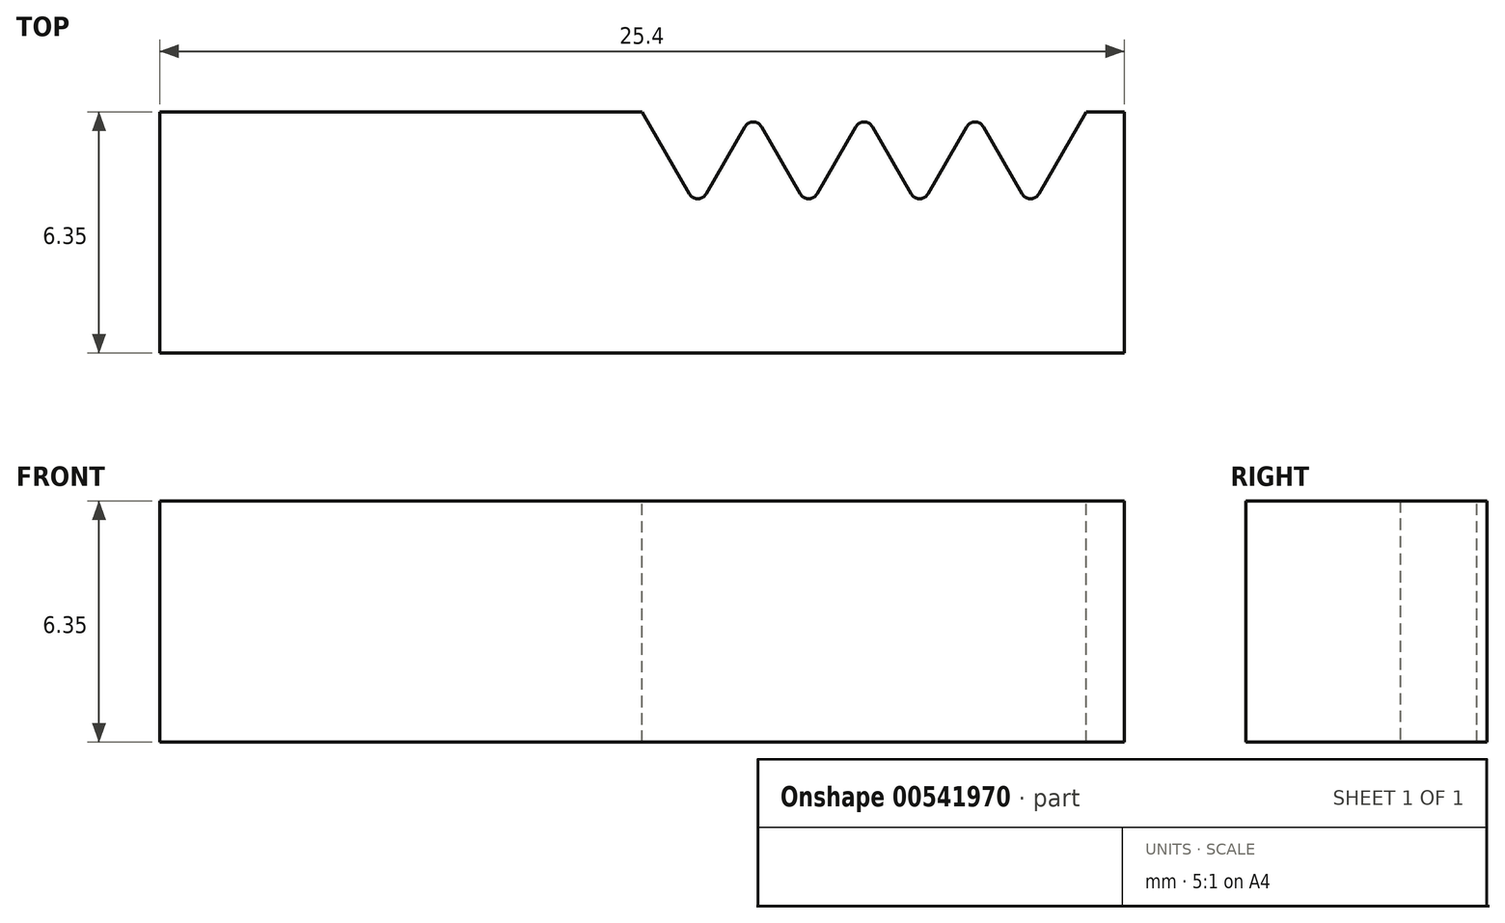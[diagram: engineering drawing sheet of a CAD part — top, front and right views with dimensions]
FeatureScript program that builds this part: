
annotation { "Feature Type Name" : "Feature", "Feature Type Description" : "" }
export const myFeature = defineFeature(function(context is Context, id is Id, definition is map)
    precondition{}
    {
        {
            var Q0;
            Q0=qCreatedBy(makeId("Top.planeOp"),FACE);
            var sketch = newSketch(context, id + "F0", { "sketchPlane" : qUnion([Q0])});
            skLineSegment(sketch, "E0", {"start": v(0, 0) * mm, "end": v(25.4, 0) * mm});
            skLineSegment(sketch, "E1", {"start": v(25.4, 0) * mm, "end": v(25.4, 6.35) * mm});
            skLineSegment(sketch, "E2", {"start": v(25.4, 6.35) * mm, "end": v(0, 6.35) * mm});
            skLineSegment(sketch, "E3", {"start": v(0, 6.35) * mm, "end": v(0, 0) * mm});
            skSolve(sketch);
        }
        {
            var Q0;
            Q0 = qSketchRegion(id + "F0", true);
            extrude(context, id + "F1", {"entities" : qUnion([Q0]), "depth" : 6.35 * mm, "offsetDistance" : 25.4 * mm});
        }
        {
            var Q0;
            Q0=makeQuery(id+"F1.opExtrude","CAP_FACE",FACE,{"disambiguationData":[OSD([sQuery(id+"F0.wireOp",EDGE,"E0"),sQuery(id+"F0.wireOp",EDGE,"E1"),sQuery(id+"F0.wireOp",EDGE,"E2"),sQuery(id+"F0.wireOp",EDGE,"E3")])],"isStart":false});
            var sketch = newSketch(context, id + "F2", { "sketchPlane" : qUnion([Q0])});
            skLineSegment(sketch, "E4", {"start": v(12.7, 0.48) * mm, "end": v(12.7, 10.56) * mm, "construction": true});
            skPoint(sketch, "E4.startSnap0", {"position": v(12.7, 0) * mm});
            skLineSegment(sketch, "E5", {"start": v(25.4, 3.81) * mm, "end": v(0, 3.8) * mm, "construction": true});
            skLineSegment(sketch, "E6", {"start": v(12.7, 6.35) * mm, "end": v(14.17, 3.8) * mm});
            skLineSegment(sketch, "E7", {"start": v(14.17, 3.8) * mm, "end": v(15.63, 6.35) * mm});
            skLineSegment(sketch, "E8.1.0.0", {"start": v(15.62, 6.35) * mm, "end": v(17.09, 3.81) * mm});
            skLineSegment(sketch, "E8.1.0.1", {"start": v(17.09, 3.8) * mm, "end": v(18.55, 6.35) * mm});
            skLineSegment(sketch, "E8.2.0.0", {"start": v(18.54, 6.35) * mm, "end": v(20, 3.81) * mm});
            skLineSegment(sketch, "E8.2.0.1", {"start": v(20, 3.8) * mm, "end": v(21.47, 6.35) * mm});
            skLineSegment(sketch, "E8.3.0.0", {"start": v(21.46, 6.35) * mm, "end": v(22.93, 3.81) * mm});
            skLineSegment(sketch, "E8.3.0.1", {"start": v(22.93, 3.81) * mm, "end": v(24.4, 6.35) * mm});
            skLineSegment(sketch, "E8.direction1", {"start": v(14.17, 3.81) * mm, "end": v(17.09, 3.81) * mm, "construction": true});
            skLineSegment(sketch, "E9", {"start": v(12.7, 6.35) * mm, "end": v(24.4, 6.35) * mm});
            skSolve(sketch);
        }
        {
            var Q0;
            Q0 = qSketchRegion(id + "F2", true);
            extrude(context, id + "F3", {"entities" : qUnion([Q0]), "operationType" : NewBodyOperationType.REMOVE, "oppositeDirection" : true, "depth" : 25.4 * mm, "offsetDistance" : 25.4 * mm});
        }
        {
            var Q0;
            Q0=makeQuery(id+"F3.boolean.opBoolean","COPY",EDGE,{"derivedFrom":makeQuery(id+"F3.opExtrude","SWEPT_EDGE",EDGE,{"disambiguationData":[OSD([sQuery(id+"F2.wireOp",EDGE,"E8.2.0.1"),sQuery(id+"F2.wireOp",EDGE,"E8.3.0.0")])]})});
            fillet(context, id + "F4", {"entities" : qUnion([Q0]), "radius" : 0.25 * mm, "tangentPropagation" : true, "allowEdgeOverflow" : false});
        }
        {
            var Q0;
            Q0=makeQuery(id+"F3.boolean.opBoolean","COPY",EDGE,{"derivedFrom":makeQuery(id+"F3.opExtrude","SWEPT_EDGE",EDGE,{"disambiguationData":[OSD([sQuery(id+"F0.wireOp",EDGE,"E2"),sQuery(id+"F2.wireOp",EDGE,"E8.3.0.1"),sQuery(id+"F2.wireOp",EDGE,"E9")])]})});
            var Q1;
            Q1=makeQuery(id+"F3.boolean.opBoolean","COPY",EDGE,{"derivedFrom":makeQuery(id+"F3.opExtrude","SWEPT_EDGE",EDGE,{"disambiguationData":[OSD([sQuery(id+"F2.wireOp",EDGE,"E8.3.0.0"),sQuery(id+"F2.wireOp",EDGE,"E8.3.0.1")])]})});
            var Q2;
            Q2=makeQuery(id+"F3.boolean.opBoolean","COPY",EDGE,{"derivedFrom":makeQuery(id+"F3.opExtrude","SWEPT_EDGE",EDGE,{"disambiguationData":[OSD([sQuery(id+"F2.wireOp",EDGE,"E8.2.0.0"),sQuery(id+"F2.wireOp",EDGE,"E8.2.0.1")])]})});
            var Q3;
            Q3=makeQuery(id+"F3.boolean.opBoolean","COPY",EDGE,{"derivedFrom":makeQuery(id+"F3.opExtrude","SWEPT_EDGE",EDGE,{"disambiguationData":[OSD([sQuery(id+"F2.wireOp",EDGE,"E8.1.0.1"),sQuery(id+"F2.wireOp",EDGE,"E8.2.0.0")])]})});
            var Q4;
            Q4=makeQuery(id+"F3.boolean.opBoolean","COPY",EDGE,{"derivedFrom":makeQuery(id+"F3.opExtrude","SWEPT_EDGE",EDGE,{"disambiguationData":[OSD([sQuery(id+"F2.wireOp",EDGE,"E8.1.0.0"),sQuery(id+"F2.wireOp",EDGE,"E8.1.0.1")])]})});
            var Q5;
            Q5=makeQuery(id+"F3.boolean.opBoolean","COPY",EDGE,{"derivedFrom":makeQuery(id+"F3.opExtrude","SWEPT_EDGE",EDGE,{"disambiguationData":[OSD([sQuery(id+"F2.wireOp",EDGE,"E7"),sQuery(id+"F2.wireOp",EDGE,"E8.1.0.0")])]})});
            var Q6;
            Q6=makeQuery(id+"F3.boolean.opBoolean","COPY",EDGE,{"derivedFrom":makeQuery(id+"F3.opExtrude","SWEPT_EDGE",EDGE,{"disambiguationData":[OSD([sQuery(id+"F2.wireOp",EDGE,"E6"),sQuery(id+"F2.wireOp",EDGE,"E7")])]})});
            fillet(context, id + "F5", {"entities" : qUnion([Q0, Q1, Q2, Q3, Q4, Q5, Q6]), "radius" : 0.25 * mm, "tangentPropagation" : true, "allowEdgeOverflow" : false});
        }
    });
